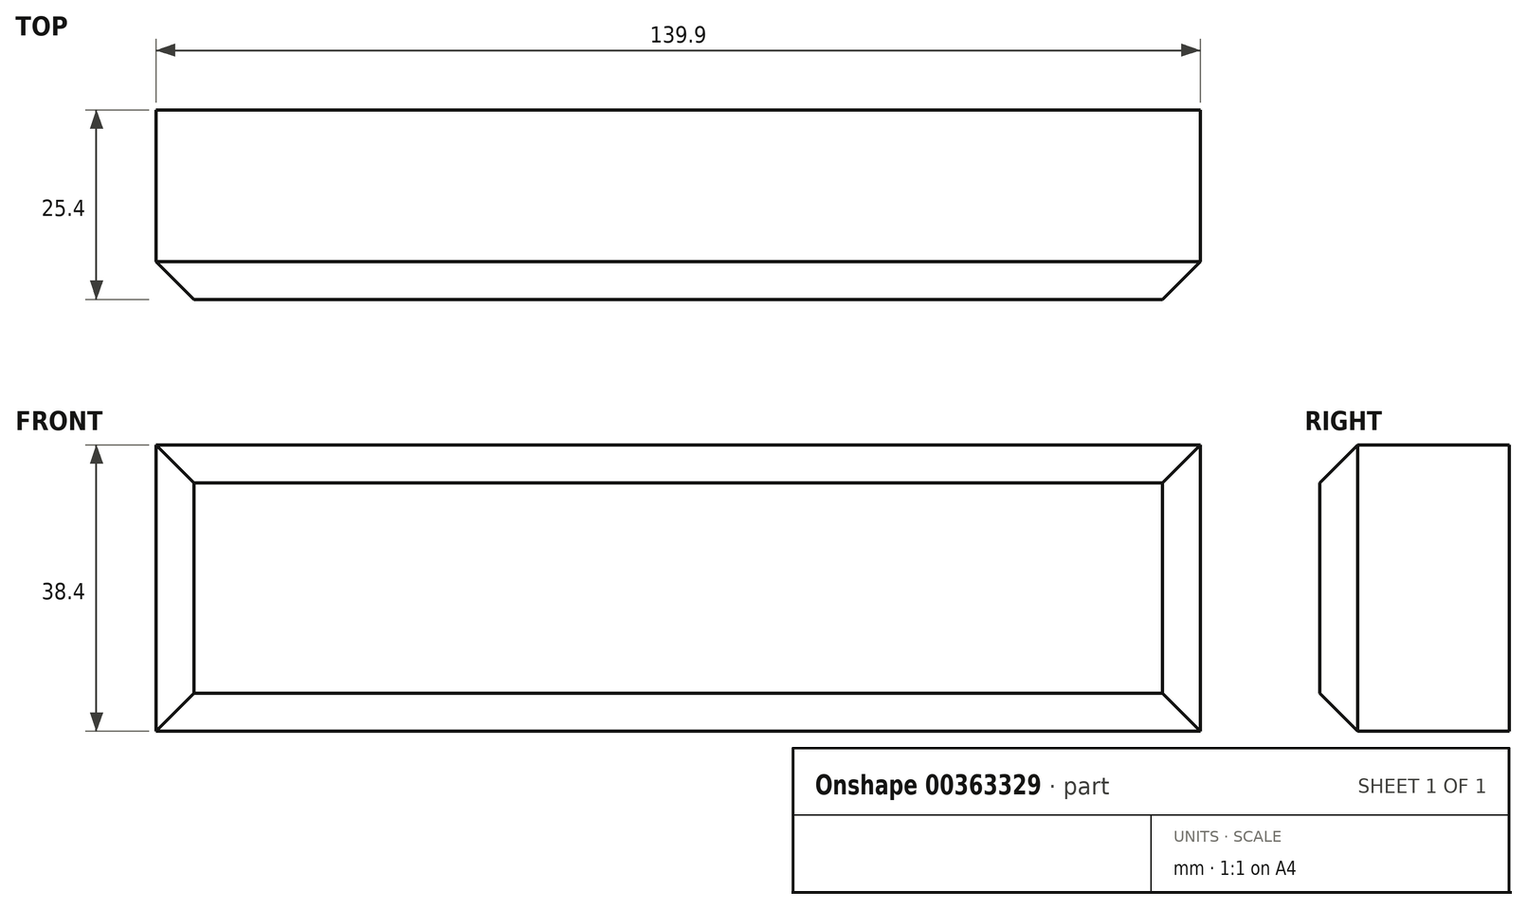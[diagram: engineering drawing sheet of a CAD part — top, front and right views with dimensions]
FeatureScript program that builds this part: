
annotation { "Feature Type Name" : "Feature", "Feature Type Description" : "" }
export const myFeature = defineFeature(function(context is Context, id is Id, definition is map)
    precondition{}
    {
        {
            var Q0;
            Q0=qCreatedBy(makeId("Front.planeOp"),FACE);
            var sketch = newSketch(context, id + "F0", { "sketchPlane" : qUnion([Q0])});
            skLineSegment(sketch, "E0.bottom", {"start": v(69.95, 19.2) * mm, "end": v(-69.95, 19.2) * mm});
            skLineSegment(sketch, "E0.top", {"start": v(69.95, -19.2) * mm, "end": v(-69.95, -19.2) * mm});
            skLineSegment(sketch, "E0.left", {"start": v(69.95, 19.2) * mm, "end": v(69.95, -19.2) * mm});
            skLineSegment(sketch, "E0.right", {"start": v(-69.95, 19.2) * mm, "end": v(-69.95, -19.2) * mm});
            skPoint(sketch, "E0.middle", {"position": v(0, 0) * mm});
            skSolve(sketch);
        }
        {
            var Q0;
            Q0=makeQuery(id+"F0.imprint","IMPRINT",FACE,{"disambiguationData":[TD([[makeQuery(id+"F0.imprint","IMPRINT",EDGE,{"derivedFrom":sQuery(id+"F0.wireOp",EDGE,"E0.bottom")}),1.0]])]});
            extrude(context, id + "F1", {"entities" : qUnion([Q0]), "depth" : 12.7 * mm});
        }
        {
            var Q0;
            Q0=makeQuery(id+"F1.opExtrude","CAP_FACE",FACE,{"disambiguationData":[OSD([sQuery(id+"F0.wireOp",EDGE,"E0.bottom"),sQuery(id+"F0.wireOp",EDGE,"E0.top"),sQuery(id+"F0.wireOp",EDGE,"E0.left"),sQuery(id+"F0.wireOp",EDGE,"E0.right")])],"isStart":true});
            extrude(context, id + "F2", {"entities" : qUnion([Q0]), "operationType" : NewBodyOperationType.ADD, "depth" : 12.7 * mm});
        }
        {
            var Q0;
            Q0=makeQuery(id+"F1.opExtrude","CAP_FACE",FACE,{"disambiguationData":[OSD([sQuery(id+"F0.wireOp",EDGE,"E0.bottom"),sQuery(id+"F0.wireOp",EDGE,"E0.top"),sQuery(id+"F0.wireOp",EDGE,"E0.left"),sQuery(id+"F0.wireOp",EDGE,"E0.right")])],"isStart":false});
            chamfer(context, id + "F3", {"entities" : qUnion([Q0]), "width" : 5.08 * mm, "tangentPropagation" : true});
        }
        {
            var Q0;
            Q0=makeQuery(id+"F1.opExtrude","CAP_FACE",FACE,{"disambiguationData":[OSD([sQuery(id+"F0.wireOp",EDGE,"E0.bottom"),sQuery(id+"F0.wireOp",EDGE,"E0.top"),sQuery(id+"F0.wireOp",EDGE,"E0.left"),sQuery(id+"F0.wireOp",EDGE,"E0.right")])],"isStart":false});
            var sketch = newSketch(context, id + "F4", { "sketchPlane" : qUnion([Q0])});
            skPoint(sketch, "E1", {"position": v(0, 0) * mm});
            skSolve(sketch);
        }
        {
            var Q0;
            {var subQ0=sQuery(id+"F0.wireOp",EDGE,"E0.right");var subQ1=sQuery(id+"F0.wireOp",EDGE,"E0.left");var subQ2=sQuery(id+"F0.wireOp",EDGE,"E0.top");var subQ3=sQuery(id+"F0.wireOp",EDGE,"E0.bottom");var subQ4=makeQuery(id+"F1.opExtrude","CAP_FACE",FACE,{"disambiguationData":[OSD([subQ3,subQ2,subQ1,subQ0])],"isStart":false});Q0=makeQuery(id+"F4.imprint","IMPRINT",FACE,{"disambiguationData":[TD([[makeQuery(id+"F4.imprint","IMPRINT",EDGE,{"derivedFrom":makeQuery(id+"F3.opChamfer","BLEND_EDGE",EDGE,{"blendedFrom":[makeQuery(id+"F1.opExtrude","CAP_EDGE",EDGE,{"disambiguationData":[OSD([subQ3])],"isStart":false}),subQ4],"blendedInto":[subQ4]})}),1.0]])]});}
            var sketch = newSketch(context, id + "F5", { "sketchPlane" : qUnion([Q0])});
            skCircle(sketch, "E2", {"center": v(0, 0) * mm, "radius": 11.99 * mm});
            skSolve(sketch);
        }
        {
            var Q0;
            Q0=sQuery(id+"F5.wireOp",EDGE,"E2");
            extrude(context, id + "F6", {"bodyType" : ToolBodyType.SURFACE, "surfaceEntities" : qUnion([Q0]), "depth" : 5.08 * mm});
        }
    });
